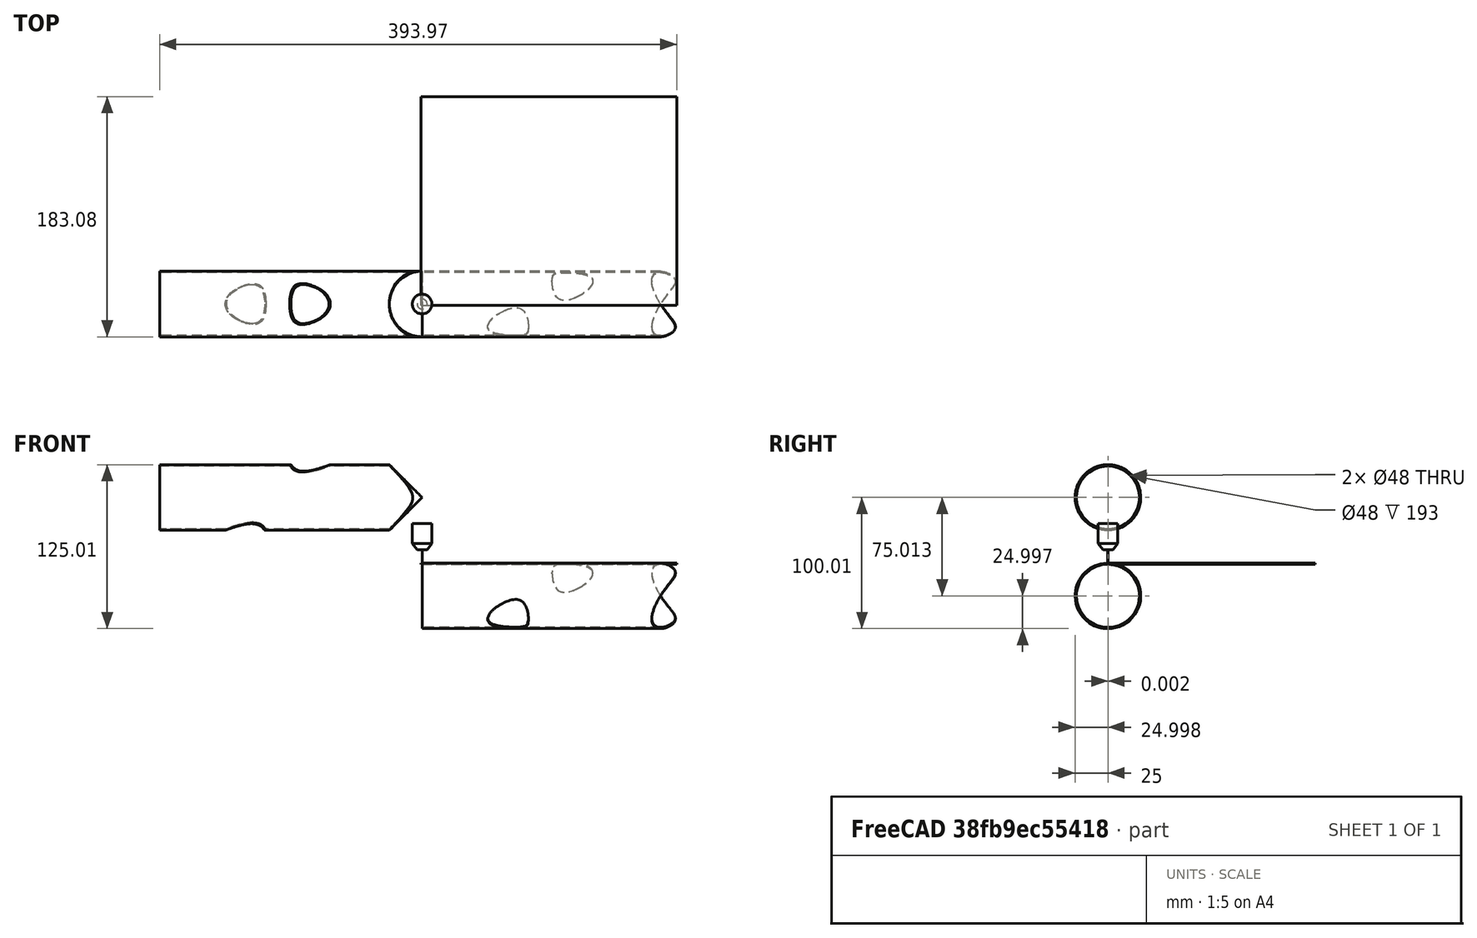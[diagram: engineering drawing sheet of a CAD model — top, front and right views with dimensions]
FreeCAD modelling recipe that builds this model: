
FCSTD DOCUMENT  (FreeCAD 0.20R25747 (Git))
Label: pipe_normalcut_path
License: All rights reserved
LicenseURL: http://en.wikipedia.org/wiki/All_rights_reserved
objects: Part::FeaturePython×7, Path::FeaturePython×4, App::DocumentObjectGroup×3, App::Link×2, Part::Offset×2, Part::Feature×2, Part::Cylinder×1, Part::MultiCommon×1, App::FeaturePython×1, Path::FeatureCompoundPython×1
note: 13 computed .brp shape members not serialized (recipe doc carries the construction recipe); baked Part::Feature solids carry a one-line shape summary decoded from their .brp

FEATURE [Part::Cylinder] Cylinder
  Angle = 360
  AttacherType = Attacher::AttachEngine3D
  FirstAngle = 45
  Height = 80
  Placement = pos=(-150,0,10) rot=(0,0,1;0rad)
  Radius = 15
  SecondAngle = 0
FEATURE [Part::FeaturePython] Tube  # WARN: FeaturePython — macro-defined, semantics opaque (R4)
  AttacherType = Attacher::AttachEngine3D
  Height = 100
  InnerRadius = 24
  OuterRadius = 25
FEATURE [Part::FeaturePython] Tube001  # WARN: FeaturePython — macro-defined, semantics opaque (R4)
  AttacherType = Attacher::AttachEngine3D
  Height = 200
  InnerRadius = 24
  OuterRadius = 25
  Placement = pos=(0,0,50) rot=(0.357407,-0.862856,-0.357407;1.71777rad)
FEATURE [Part::FeaturePython] Cutout  # WARN: FeaturePython — macro-defined, semantics opaque (R4)
  Base = -> Tube001
  Tolerance = 0
  Tool = -> Tube
FEATURE [Part::FeaturePython] Cutout001  # WARN: FeaturePython — macro-defined, semantics opaque (R4)
  Base = -> Cutout
  Tolerance = 0
  Tool = -> Cylinder
FEATURE [App::Link] Link  label="Cutout002"
  LinkTransform = true
  LinkedObject = -> Cutout001 [Face1]
FEATURE [App::Link] Link001  label="Cutout003"
  LinkTransform = true
  LinkedObject = -> Cutout001 [Face6]
FEATURE [Part::Offset] Offset
  Fill = true
  Intersection = false
  Join = 0
  Mode = 0
  SelfIntersection = false
  Source = -> Link
  Value = -1
FEATURE [Part::Offset] Offset001
  Fill = true
  Intersection = false
  Join = 0
  Mode = 0
  SelfIntersection = false
  Source = -> Link001
  Value = -1
FEATURE [Part::MultiCommon] Common
  Shapes = -> [Offset,Offset001]
FEATURE [App::DocumentObjectGroup] Group  label="Model"
  Group = -> [Cutout001,Common]
FEATURE [Part::Feature] Common001  label="RotatedAndTranslatedCopy"
  Placement = pos=(200,-35.357,-60.368) rot=(-1,0,0;0.785398rad)
  shape: bbox 193 x 67.04 x 62.1 mm, 12 faces (baked)
FEATURE [Part::Feature] Shape
  shape: bbox 193 x 157.1 x 2e-07 mm, 0 faces, 0 solids (baked)
FEATURE [App::FeaturePython] SetupSheet  # Path/CAM operation (typed FeaturePython)
  ClearanceHeightExpression = OpStockZMax+SetupSheet.ClearanceHeightOffset
  ClearanceHeightOffset = 5
  CoolantMode = 0
  CoolantModes = None | Flood | Mist
  FinalDepthExpression = OpFinalDepth
  HorizRapid = 0
  SafeHeightExpression = OpStockZMax+SetupSheet.SafeHeightOffset
  SafeHeightOffset = 3
  StartDepthExpression = OpStartDepth
  StepDownExpression = OpToolDiameter
  VertRapid = 0
FEATURE [Part::FeaturePython] Clone  label="Model-Shape"  # Draft clone (typed FeaturePython)
  AttacherType = Attacher::AttachEngine3D
  Fuse = false
  Objects = -> [Shape]
  PathResource = Model
  Scale = (1,1,1)
FEATURE [App::DocumentObjectGroup] Model  label="Model001"
  Group = -> [Clone]
FEATURE [Part::FeaturePython] Stock  # WARN: FeaturePython — macro-defined, semantics opaque (R4)
  Base = -> Model
  ExtXneg = 1
  ExtXpos = 1
  ExtYneg = 1
  ExtYpos = 1
  ExtZneg = 1
  ExtZpos = 0
  Placement = pos=(0,-0.00166094,-0.0126609) rot=(0,0,1;0rad)
  StockType = FromBase
FEATURE [Part::FeaturePython] ToolBit001  label="100um laser"  # Path/CAM toolbit (typed FeaturePython)
  BitPropertyNames = Chipload | CuttingEdgeHeight | Diameter | Flutes | Length | Material | ShankDiameter
  BitShape = <userpath>/Documents/GitHub/FreeCADBuild/Mod/Path/Tools\Shape\laser.fcstd
  Chipload = 0
  CuttingEdgeHeight = 10
  Diameter = 0.1
  File = <userpath>/Documents/GitHub/FreeCADBuild/Mod/Path/Tools/Bit/100um_laser.fctb
  Flutes = 0
  Length = 30
  Material = 0
  ShankDiameter = 15
  ShapeName = laser
FEATURE [Path::FeaturePython] _00um_laser  label="100um laser001"  # Path/CAM operation (typed FeaturePython)
  HorizFeed = 0
  HorizRapid = 0
  SpindleDir = 0
  SpindleSpeed = 0
  Tool = -> ToolBit001
  ToolNumber = 2
  VertFeed = 0
  VertRapid = 0
  expr: HorizRapid = SetupSheet.HorizRapid
  expr: VertRapid = SetupSheet.VertRapid
FEATURE [App::DocumentObjectGroup] Tools
  Group = -> [_00um_laser]
FEATURE [Path::FeaturePython] Engrave  # Path/CAM operation (typed FeaturePython)
  Active = true
  Base = -> [Clone]
  ClearanceHeight = 4.98734
  CoolantMode = None
  CycleTime = Cycletime Error
  FinalDepth = -0.112661
  OpFinalDepth = -0.112661
  OpStartDepth = -0.0126609
  OpStockZMax = -0.0126609
  OpStockZMin = -1.01266
  OpToolDiameter = 0.1
  SafeHeight = 2.98734
  StartDepth = -0.0126609
  StartVertex = 0
  StepDown = 0.1
  ToolController = -> _00um_laser
  expr: ClearanceHeight = OpStockZMax + SetupSheet.ClearanceHeightOffset
  expr: SafeHeight = OpStockZMax + SetupSheet.SafeHeightOffset
  expr: StepDown = OpToolDiameter
  expr: FinalDepth = OpFinalDepth
  expr: StartDepth = OpStartDepth
FEATURE [Path::FeaturePython] AxisMapDressup  # Path/CAM operation (typed FeaturePython)
  AxisMap = 1
  Base = -> Engrave
  Radius = 25
FEATURE [Path::FeatureCompoundPython] Operations  # Path/CAM operation (typed FeaturePython)
  Group = -> [AxisMapDressup]
  UsePlacements = false
FEATURE [Path::FeaturePython] Job  # Path/CAM operation (typed FeaturePython)
  CycleTime = 00:00:00
  Fixtures = G54
  GeometryTolerance = 0.01
  Model = -> Model
  Operations = -> Operations
  OrderOutputBy = 0
  PostProcessor = 7
  SetupSheet = -> SetupSheet
  SplitOutput = false
  Stock = -> Stock
  Tools = -> Tools
